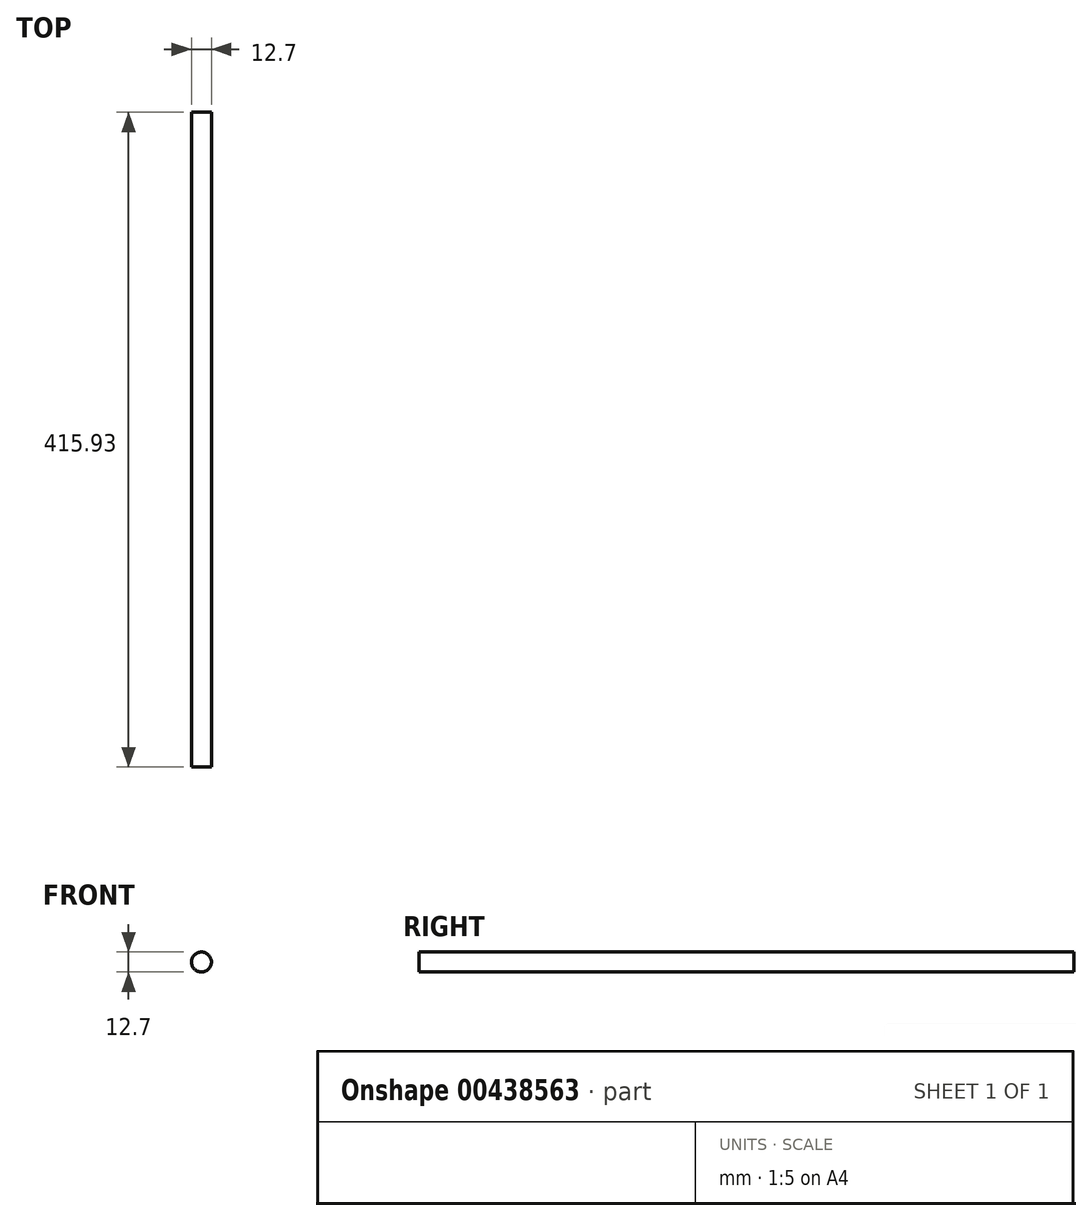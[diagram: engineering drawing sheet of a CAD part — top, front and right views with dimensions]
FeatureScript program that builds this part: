
annotation { "Feature Type Name" : "Feature", "Feature Type Description" : "" }
export const myFeature = defineFeature(function(context is Context, id is Id, definition is map)
    precondition{}
    {
        {
            var Q0;
            Q0=qCreatedBy(makeId("Front.planeOp"),FACE);
            var sketch = newSketch(context, id + "F0", { "sketchPlane" : qUnion([Q0])});
            skCircle(sketch, "E0", {"center": v(0, 0) * mm, "radius": 6.35 * mm});
            skSolve(sketch);
        }
        {
            var Q0;
            Q0=makeQuery(id+"F0.imprint","IMPRINT",FACE,{"disambiguationData":[TD([[makeQuery(id+"F0.imprint","IMPRINT",EDGE,{"derivedFrom":sQuery(id+"F0.wireOp",EDGE,"E0")}),1.0]])]});
            extrude(context, id + "F1", {"entities" : qUnion([Q0]), "depth" : 415.92 * mm});
        }
    });
